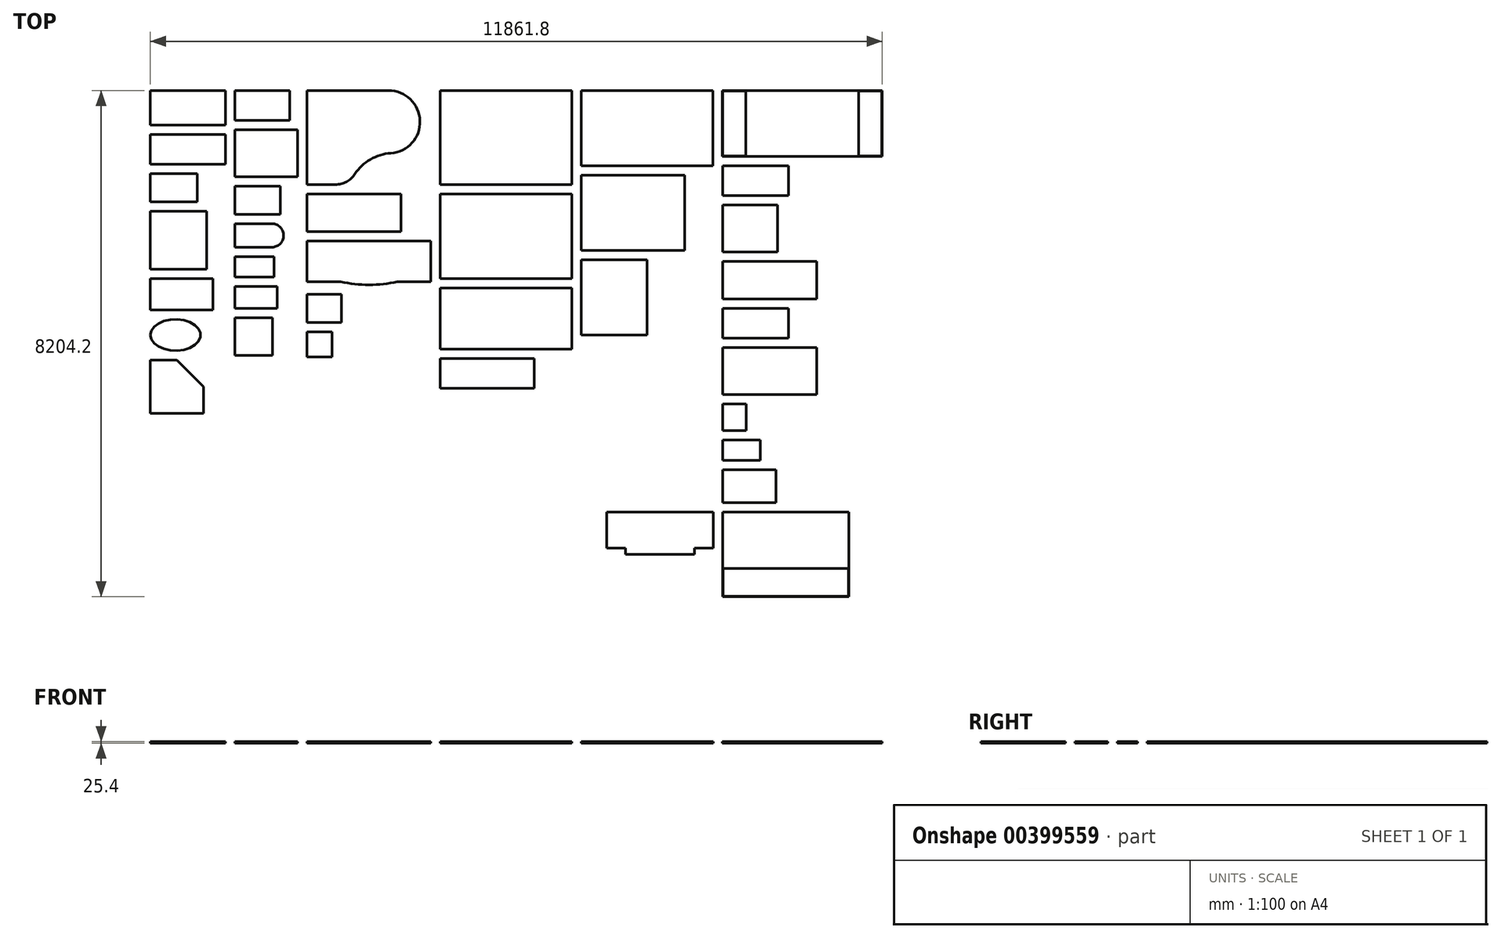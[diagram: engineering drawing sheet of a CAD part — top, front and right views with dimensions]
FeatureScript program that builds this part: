
annotation { "Feature Type Name" : "Feature", "Feature Type Description" : "" }
export const myFeature = defineFeature(function(context is Context, id is Id, definition is map)
    precondition{}
    {
        {
            var Q0;
            Q0=qCreatedBy(makeId("Top.planeOp"),FACE);
            var sketch = newSketch(context, id + "F0", { "sketchPlane" : qUnion([Q0])});
            skLineSegment(sketch, "E0.bottom", {"start": v(0, 0) * mm, "end": v(1219.2, 0) * mm});
            skLineSegment(sketch, "E0.top", {"start": v(0, -558.8) * mm, "end": v(1219.2, -558.8) * mm});
            skLineSegment(sketch, "E0.left", {"start": v(0, 0) * mm, "end": v(0, -558.8) * mm});
            skLineSegment(sketch, "E0.right", {"start": v(1219.2, 0) * mm, "end": v(1219.2, -558.8) * mm});
            skLineSegment(sketch, "E1.bottom", {"start": v(0, -711.2) * mm, "end": v(1219.2, -711.2) * mm});
            skLineSegment(sketch, "E1.top", {"start": v(0, -1193.8) * mm, "end": v(1219.2, -1193.8) * mm});
            skLineSegment(sketch, "E1.left", {"start": v(0, -711.2) * mm, "end": v(0, -1193.8) * mm});
            skLineSegment(sketch, "E1.right", {"start": v(1219.2, -711.2) * mm, "end": v(1219.2, -1193.8) * mm});
            skLineSegment(sketch, "E2.bottom", {"start": v(0, -1346.2) * mm, "end": v(762, -1346.2) * mm});
            skLineSegment(sketch, "E2.top", {"start": v(0, -1803.4) * mm, "end": v(762, -1803.4) * mm});
            skLineSegment(sketch, "E2.left", {"start": v(0, -1346.2) * mm, "end": v(0, -1803.4) * mm});
            skLineSegment(sketch, "E2.right", {"start": v(762, -1346.2) * mm, "end": v(762, -1803.4) * mm});
            skLineSegment(sketch, "E3.bottom", {"start": v(0, -1955.8) * mm, "end": v(914.4, -1955.8) * mm});
            skLineSegment(sketch, "E3.top", {"start": v(0, -2895.6) * mm, "end": v(914.4, -2895.6) * mm});
            skLineSegment(sketch, "E3.left", {"start": v(0, -1955.8) * mm, "end": v(0, -2895.6) * mm});
            skLineSegment(sketch, "E3.right", {"start": v(914.4, -1955.8) * mm, "end": v(914.4, -2895.6) * mm});
            skLineSegment(sketch, "E4.bottom", {"start": v(0, -3048) * mm, "end": v(1016, -3048) * mm});
            skLineSegment(sketch, "E4.top", {"start": v(0, -3556) * mm, "end": v(1016, -3556) * mm});
            skLineSegment(sketch, "E4.left", {"start": v(0, -3048) * mm, "end": v(0, -3556) * mm});
            skLineSegment(sketch, "E4.right", {"start": v(1016, -3048) * mm, "end": v(1016, -3556) * mm});
            skEllipse(sketch, "E5", {"center": v(406.4, -3962.4) * mm, "majorRadius": 406.4 * mm, "minorRadius": 254 * mm, "majorAxis": v(-1, 0)});
            skLineSegment(sketch, "E6", {"start": v(0, -3962.4) * mm, "end": v(812.8, -3962.4) * mm, "construction": true});
            skLineSegment(sketch, "E7", {"start": v(406.4, -3708.4) * mm, "end": v(406.4, -4216.4) * mm, "construction": true});
            skLineSegment(sketch, "E8.bottom", {"start": v(1371.6, 0) * mm, "end": v(2260.6, 0) * mm});
            skLineSegment(sketch, "E8.top", {"start": v(1371.6, -482.6) * mm, "end": v(2260.6, -482.6) * mm});
            skLineSegment(sketch, "E8.left", {"start": v(1371.6, 0) * mm, "end": v(1371.6, -482.6) * mm});
            skLineSegment(sketch, "E8.right", {"start": v(2260.6, 0) * mm, "end": v(2260.6, -482.6) * mm});
            skLineSegment(sketch, "E9.bottom", {"start": v(1371.6, -635) * mm, "end": v(2387.6, -635) * mm});
            skLineSegment(sketch, "E9.top", {"start": v(1371.6, -1397) * mm, "end": v(2387.6, -1397) * mm});
            skLineSegment(sketch, "E9.left", {"start": v(1371.6, -635) * mm, "end": v(1371.6, -1397) * mm});
            skLineSegment(sketch, "E9.right", {"start": v(2387.6, -635) * mm, "end": v(2387.6, -1397) * mm});
            skLineSegment(sketch, "E10.bottom", {"start": v(1371.6, -1549.4) * mm, "end": v(2108.2, -1549.4) * mm});
            skLineSegment(sketch, "E10.top", {"start": v(1371.6, -2006.6) * mm, "end": v(2108.2, -2006.6) * mm});
            skLineSegment(sketch, "E10.left", {"start": v(1371.6, -1549.4) * mm, "end": v(1371.6, -2006.6) * mm});
            skLineSegment(sketch, "E10.right", {"start": v(2108.2, -1549.4) * mm, "end": v(2108.2, -2006.6) * mm});
            skLineSegment(sketch, "E11.bottom", {"start": v(1371.6, -2159) * mm, "end": v(1968.5, -2159) * mm});
            skLineSegment(sketch, "E11.top", {"start": v(1371.6, -2540) * mm, "end": v(1968.5, -2540) * mm});
            skLineSegment(sketch, "E11.left", {"start": v(1371.6, -2159) * mm, "end": v(1371.6, -2540) * mm});
            skLineSegment(sketch, "E11.right", {"start": v(1968.5, -2159) * mm, "end": v(1968.5, -2540) * mm, "construction": true});
            skArc(sketch, "E12", {"start": v(1968.5, -2159) * mm, "mid": v(2159, -2349.5) * mm, "end": v(1968.5, -2540) * mm});
            skLineSegment(sketch, "E13.bottom", {"start": v(1371.6, -2692.4) * mm, "end": v(2006.6, -2692.4) * mm});
            skLineSegment(sketch, "E13.top", {"start": v(1371.6, -3022.6) * mm, "end": v(2006.6, -3022.6) * mm});
            skLineSegment(sketch, "E13.left", {"start": v(1371.6, -2692.4) * mm, "end": v(1371.6, -3022.6) * mm});
            skLineSegment(sketch, "E13.right", {"start": v(2006.6, -2692.4) * mm, "end": v(2006.6, -3022.6) * mm});
            skLineSegment(sketch, "E14.bottom", {"start": v(1371.6, -3175) * mm, "end": v(2057.4, -3175) * mm});
            skLineSegment(sketch, "E14.top", {"start": v(1371.6, -3530.6) * mm, "end": v(2057.4, -3530.6) * mm});
            skLineSegment(sketch, "E14.left", {"start": v(1371.6, -3175) * mm, "end": v(1371.6, -3530.6) * mm});
            skLineSegment(sketch, "E14.right", {"start": v(2057.4, -3175) * mm, "end": v(2057.4, -3530.6) * mm});
            skLineSegment(sketch, "E15.bottom", {"start": v(1371.6, -3683) * mm, "end": v(1981.2, -3683) * mm});
            skLineSegment(sketch, "E15.top", {"start": v(1371.6, -4292.6) * mm, "end": v(1981.2, -4292.6) * mm});
            skLineSegment(sketch, "E15.left", {"start": v(1371.6, -3683) * mm, "end": v(1371.6, -4292.6) * mm});
            skLineSegment(sketch, "E15.right", {"start": v(1981.2, -3683) * mm, "end": v(1981.2, -4292.6) * mm});
            skLineSegment(sketch, "E16", {"start": v(2540, 0) * mm, "end": v(2540, -1524) * mm});
            skLineSegment(sketch, "E17", {"start": v(2540, -1524) * mm, "end": v(2997.2, -1524) * mm});
            skLineSegment(sketch, "E18", {"start": v(2540, 0) * mm, "end": v(3860.8, 0) * mm});
            skArc(sketch, "E19", {"start": v(3860.8, 0) * mm, "mid": v(4368.49, -490.22) * mm, "end": v(3896.34, -1014.76) * mm});
            skArc(sketch, "E20", {"start": v(3896.34, -1014.76) * mm, "mid": v(3566.06, -1116.48) * mm, "end": v(3314.68, -1353.63) * mm});
            skArc(sketch, "E21", {"start": v(3314.68, -1353.63) * mm, "mid": v(3177.35, -1478.72) * mm, "end": v(2997.2, -1524) * mm});
            skLineSegment(sketch, "E22.bottom", {"start": v(2540, -1676.4) * mm, "end": v(4064, -1676.4) * mm});
            skLineSegment(sketch, "E22.top", {"start": v(2540, -2286) * mm, "end": v(4064, -2286) * mm});
            skLineSegment(sketch, "E22.left", {"start": v(2540, -1676.4) * mm, "end": v(2540, -2286) * mm});
            skLineSegment(sketch, "E22.right", {"start": v(4064, -1676.4) * mm, "end": v(4064, -2286) * mm});
            skLineSegment(sketch, "E23", {"start": v(3086.1, -3098.8) * mm, "end": v(2540, -3098.8) * mm});
            skLineSegment(sketch, "E24", {"start": v(2540, -3098.8) * mm, "end": v(2540, -2438.4) * mm});
            skLineSegment(sketch, "E25", {"start": v(2540, -2438.4) * mm, "end": v(4546.6, -2438.4) * mm});
            skLineSegment(sketch, "E26", {"start": v(4546.6, -2438.4) * mm, "end": v(4546.6, -3098.8) * mm});
            skLineSegment(sketch, "E27", {"start": v(4546.6, -3098.8) * mm, "end": v(4000.5, -3098.8) * mm});
            skArc(sketch, "E28", {"start": v(3086.1, -3098.8) * mm, "mid": v(3543.3, -3149.6) * mm, "end": v(4000.5, -3098.8) * mm});
            skLineSegment(sketch, "E29.bottom", {"start": v(2540, -3302) * mm, "end": v(3098.8, -3302) * mm});
            skLineSegment(sketch, "E29.top", {"start": v(2540, -3759.2) * mm, "end": v(3098.8, -3759.2) * mm});
            skLineSegment(sketch, "E29.left", {"start": v(2540, -3302) * mm, "end": v(2540, -3759.2) * mm});
            skLineSegment(sketch, "E29.right", {"start": v(3098.8, -3302) * mm, "end": v(3098.8, -3759.2) * mm});
            skLineSegment(sketch, "E30.bottom", {"start": v(2540, -3911.6) * mm, "end": v(2946.4, -3911.6) * mm});
            skLineSegment(sketch, "E30.top", {"start": v(2540, -4318) * mm, "end": v(2946.4, -4318) * mm});
            skLineSegment(sketch, "E30.left", {"start": v(2540, -3911.6) * mm, "end": v(2540, -4318) * mm});
            skLineSegment(sketch, "E30.right", {"start": v(2946.4, -3911.6) * mm, "end": v(2946.4, -4318) * mm});
            skLineSegment(sketch, "E31.bottom", {"start": v(4699, 0) * mm, "end": v(6832.6, 0) * mm});
            skLineSegment(sketch, "E31.top", {"start": v(4699, -1524) * mm, "end": v(6832.6, -1524) * mm});
            skLineSegment(sketch, "E31.left", {"start": v(4699, 0) * mm, "end": v(4699, -1524) * mm});
            skLineSegment(sketch, "E31.right", {"start": v(6832.6, 0) * mm, "end": v(6832.6, -1524) * mm});
            skLineSegment(sketch, "E32.bottom", {"start": v(4699, -1676.4) * mm, "end": v(6832.6, -1676.4) * mm});
            skLineSegment(sketch, "E32.top", {"start": v(4699, -3048) * mm, "end": v(6832.6, -3048) * mm});
            skLineSegment(sketch, "E32.left", {"start": v(4699, -1676.4) * mm, "end": v(4699, -3048) * mm});
            skLineSegment(sketch, "E32.right", {"start": v(6832.6, -1676.4) * mm, "end": v(6832.6, -3048) * mm});
            skLineSegment(sketch, "E33.bottom", {"start": v(4699, -3200.4) * mm, "end": v(6832.6, -3200.4) * mm});
            skLineSegment(sketch, "E33.top", {"start": v(4699, -4191) * mm, "end": v(6832.6, -4191) * mm});
            skLineSegment(sketch, "E33.left", {"start": v(4699, -3200.4) * mm, "end": v(4699, -4191) * mm});
            skLineSegment(sketch, "E33.right", {"start": v(6832.6, -3200.4) * mm, "end": v(6832.6, -4191) * mm});
            skLineSegment(sketch, "E34.bottom", {"start": v(6985, 0) * mm, "end": v(9118.6, 0) * mm});
            skLineSegment(sketch, "E34.top", {"start": v(6985, -1219.2) * mm, "end": v(9118.6, -1219.2) * mm});
            skLineSegment(sketch, "E34.left", {"start": v(6985, 0) * mm, "end": v(6985, -1219.2) * mm});
            skLineSegment(sketch, "E34.right", {"start": v(9118.6, 0) * mm, "end": v(9118.6, -1219.2) * mm});
            skLineSegment(sketch, "E35.bottom", {"start": v(6985, -1371.6) * mm, "end": v(8661.4, -1371.6) * mm});
            skLineSegment(sketch, "E35.top", {"start": v(6985, -2590.8) * mm, "end": v(8661.4, -2590.8) * mm});
            skLineSegment(sketch, "E35.left", {"start": v(6985, -1371.6) * mm, "end": v(6985, -2590.8) * mm});
            skLineSegment(sketch, "E35.right", {"start": v(8661.4, -1371.6) * mm, "end": v(8661.4, -2590.8) * mm});
            skLineSegment(sketch, "E36.bottom", {"start": v(6985, -2743.2) * mm, "end": v(8051.8, -2743.2) * mm});
            skLineSegment(sketch, "E36.top", {"start": v(6985, -3962.4) * mm, "end": v(8051.8, -3962.4) * mm});
            skLineSegment(sketch, "E36.left", {"start": v(6985, -2743.2) * mm, "end": v(6985, -3962.4) * mm});
            skLineSegment(sketch, "E36.right", {"start": v(8051.8, -2743.2) * mm, "end": v(8051.8, -3962.4) * mm});
            skLineSegment(sketch, "E37.bottom", {"start": v(9271, 0) * mm, "end": v(11861.8, 0) * mm});
            skLineSegment(sketch, "E37.top", {"start": v(9271, -1066.8) * mm, "end": v(11861.8, -1066.8) * mm});
            skLineSegment(sketch, "E37.left", {"start": v(9271, 0) * mm, "end": v(9271, -1066.8) * mm});
            skLineSegment(sketch, "E37.right", {"start": v(11861.8, 0) * mm, "end": v(11861.8, -1066.8) * mm});
            skLineSegment(sketch, "E38.bottom", {"start": v(9277.35, -6.35) * mm, "end": v(9652, -6.35) * mm});
            skLineSegment(sketch, "E38.top", {"start": v(9277.35, -1060.45) * mm, "end": v(9652, -1060.45) * mm});
            skLineSegment(sketch, "E38.left", {"start": v(9277.35, -6.35) * mm, "end": v(9277.35, -1060.45) * mm});
            skLineSegment(sketch, "E38.right", {"start": v(9652, -6.35) * mm, "end": v(9652, -1060.45) * mm});
            skLineSegment(sketch, "E39.bottom", {"start": v(11480.8, -6.35) * mm, "end": v(11855.45, -6.35) * mm});
            skLineSegment(sketch, "E39.top", {"start": v(11480.8, -1060.45) * mm, "end": v(11855.45, -1060.45) * mm});
            skLineSegment(sketch, "E39.left", {"start": v(11480.8, -6.35) * mm, "end": v(11480.8, -1060.45) * mm});
            skLineSegment(sketch, "E39.right", {"start": v(11855.45, -6.35) * mm, "end": v(11855.45, -1060.45) * mm});
            skLineSegment(sketch, "E40.bottom", {"start": v(9277.35, -1219.2) * mm, "end": v(10344.15, -1219.2) * mm});
            skLineSegment(sketch, "E40.top", {"start": v(9277.35, -1701.8) * mm, "end": v(10344.15, -1701.8) * mm});
            skLineSegment(sketch, "E40.left", {"start": v(9277.35, -1219.2) * mm, "end": v(9277.35, -1701.8) * mm});
            skLineSegment(sketch, "E40.right", {"start": v(10344.15, -1219.2) * mm, "end": v(10344.15, -1701.8) * mm});
            skLineSegment(sketch, "E41.bottom", {"start": v(9277.35, -1854.2) * mm, "end": v(10166.35, -1854.2) * mm});
            skLineSegment(sketch, "E41.top", {"start": v(9277.35, -2616.2) * mm, "end": v(10166.35, -2616.2) * mm});
            skLineSegment(sketch, "E41.left", {"start": v(9277.35, -1854.2) * mm, "end": v(9277.35, -2616.2) * mm});
            skLineSegment(sketch, "E41.right", {"start": v(10166.35, -1854.2) * mm, "end": v(10166.35, -2616.2) * mm});
            skLineSegment(sketch, "E42.bottom", {"start": v(9277.35, -2768.6) * mm, "end": v(10801.35, -2768.6) * mm});
            skLineSegment(sketch, "E42.top", {"start": v(9277.35, -3378.2) * mm, "end": v(10801.35, -3378.2) * mm});
            skLineSegment(sketch, "E42.left", {"start": v(9277.35, -2768.6) * mm, "end": v(9277.35, -3378.2) * mm});
            skLineSegment(sketch, "E42.right", {"start": v(10801.35, -2768.6) * mm, "end": v(10801.35, -3378.2) * mm});
            skLineSegment(sketch, "E43.bottom", {"start": v(9277.35, -3530.6) * mm, "end": v(10344.15, -3530.6) * mm});
            skLineSegment(sketch, "E43.top", {"start": v(9277.35, -4013.2) * mm, "end": v(10344.15, -4013.2) * mm});
            skLineSegment(sketch, "E43.left", {"start": v(9277.35, -3530.6) * mm, "end": v(9277.35, -4013.2) * mm});
            skLineSegment(sketch, "E43.right", {"start": v(10344.15, -3530.6) * mm, "end": v(10344.15, -4013.2) * mm});
            skLineSegment(sketch, "E44.bottom", {"start": v(9277.35, -4165.6) * mm, "end": v(10801.35, -4165.6) * mm});
            skLineSegment(sketch, "E44.top", {"start": v(9277.35, -4927.6) * mm, "end": v(10801.35, -4927.6) * mm});
            skLineSegment(sketch, "E44.left", {"start": v(9277.35, -4165.6) * mm, "end": v(9277.35, -4927.6) * mm});
            skLineSegment(sketch, "E44.right", {"start": v(10801.35, -4165.6) * mm, "end": v(10801.35, -4927.6) * mm});
            skLineSegment(sketch, "E45.bottom", {"start": v(9277.35, -5080) * mm, "end": v(9658.35, -5080) * mm});
            skLineSegment(sketch, "E45.top", {"start": v(9277.35, -5511.8) * mm, "end": v(9658.35, -5511.8) * mm});
            skLineSegment(sketch, "E45.left", {"start": v(9277.35, -5080) * mm, "end": v(9277.35, -5511.8) * mm});
            skLineSegment(sketch, "E45.right", {"start": v(9658.35, -5080) * mm, "end": v(9658.35, -5511.8) * mm});
            skLineSegment(sketch, "E46.bottom", {"start": v(9277.35, -5664.2) * mm, "end": v(9886.95, -5664.2) * mm});
            skLineSegment(sketch, "E46.top", {"start": v(9277.35, -5994.4) * mm, "end": v(9886.95, -5994.4) * mm});
            skLineSegment(sketch, "E46.left", {"start": v(9277.35, -5664.2) * mm, "end": v(9277.35, -5994.4) * mm});
            skLineSegment(sketch, "E46.right", {"start": v(9886.95, -5664.2) * mm, "end": v(9886.95, -5994.4) * mm});
            skLineSegment(sketch, "E47.bottom", {"start": v(9277.35, -6146.8) * mm, "end": v(10140.95, -6146.8) * mm});
            skLineSegment(sketch, "E47.top", {"start": v(9277.35, -6680.2) * mm, "end": v(10140.95, -6680.2) * mm});
            skLineSegment(sketch, "E47.left", {"start": v(9277.35, -6146.8) * mm, "end": v(9277.35, -6680.2) * mm});
            skLineSegment(sketch, "E47.right", {"start": v(10140.95, -6146.8) * mm, "end": v(10140.95, -6680.2) * mm});
            skLineSegment(sketch, "E48.bottom", {"start": v(9277.35, -6832.6) * mm, "end": v(11322.05, -6832.6) * mm});
            skLineSegment(sketch, "E48.top", {"start": v(9277.35, -8204.2) * mm, "end": v(11322.05, -8204.2) * mm});
            skLineSegment(sketch, "E48.left", {"start": v(9277.35, -6832.6) * mm, "end": v(9277.35, -8204.2) * mm});
            skLineSegment(sketch, "E48.right", {"start": v(11322.05, -6832.6) * mm, "end": v(11322.05, -8204.2) * mm});
            skLineSegment(sketch, "E49.bottom", {"start": v(9283.7, -7747) * mm, "end": v(11315.7, -7747) * mm});
            skLineSegment(sketch, "E49.top", {"start": v(9283.7, -8197.85) * mm, "end": v(11315.7, -8197.85) * mm});
            skLineSegment(sketch, "E49.left", {"start": v(9283.7, -7747) * mm, "end": v(9283.7, -8197.85) * mm});
            skLineSegment(sketch, "E49.right", {"start": v(11315.7, -7747) * mm, "end": v(11315.7, -8197.85) * mm});
            skLineSegment(sketch, "E50.bottom", {"start": v(9124.95, -6832.6) * mm, "end": v(7397.75, -6832.6) * mm});
            skLineSegment(sketch, "E50.top", {"start": v(9124.95, -7416.8) * mm, "end": v(8820.15, -7416.8) * mm});
            skLineSegment(sketch, "E50.left", {"start": v(9124.95, -6832.6) * mm, "end": v(9124.95, -7416.8) * mm});
            skLineSegment(sketch, "E50.right", {"start": v(7397.75, -6832.6) * mm, "end": v(7397.75, -7416.8) * mm});
            skLineSegment(sketch, "E51", {"start": v(7702.55, -7416.8) * mm, "end": v(7702.55, -7518.4) * mm});
            skLineSegment(sketch, "E52", {"start": v(7702.55, -7518.4) * mm, "end": v(8820.15, -7518.4) * mm});
            skLineSegment(sketch, "E53", {"start": v(8820.15, -7518.4) * mm, "end": v(8820.15, -7416.8) * mm});
            skLineSegment(sketch, "E54.trimOffspring", {"start": v(7702.55, -7416.8) * mm, "end": v(7397.75, -7416.8) * mm});
            skLineSegment(sketch, "E55", {"start": v(0, -4368.8) * mm, "end": v(431.05, -4368.8) * mm});
            skLineSegment(sketch, "E56", {"start": v(431.05, -4368.8) * mm, "end": v(863.6, -4801.35) * mm});
            skLineSegment(sketch, "E57", {"start": v(863.6, -4801.35) * mm, "end": v(863.6, -5232.4) * mm});
            skLineSegment(sketch, "E58", {"start": v(863.6, -5232.4) * mm, "end": v(0, -5232.4) * mm});
            skLineSegment(sketch, "E59", {"start": v(0, -5232.4) * mm, "end": v(0, -4368.8) * mm});
            skLineSegment(sketch, "E60.bottom", {"start": v(4699, -4343.4) * mm, "end": v(6223, -4343.4) * mm});
            skLineSegment(sketch, "E60.top", {"start": v(4699, -4826) * mm, "end": v(6223, -4826) * mm});
            skLineSegment(sketch, "E60.left", {"start": v(4699, -4343.4) * mm, "end": v(4699, -4826) * mm});
            skLineSegment(sketch, "E60.right", {"start": v(6223, -4343.4) * mm, "end": v(6223, -4826) * mm});
            skSolve(sketch);
        }
        {
            var Q0;
            Q0=qSketchRegion(id+"F0",true);
            extrude(context, id + "F1", {"entities" : qUnion([Q0]), "depth" : 25.4 * mm});
        }
    });
